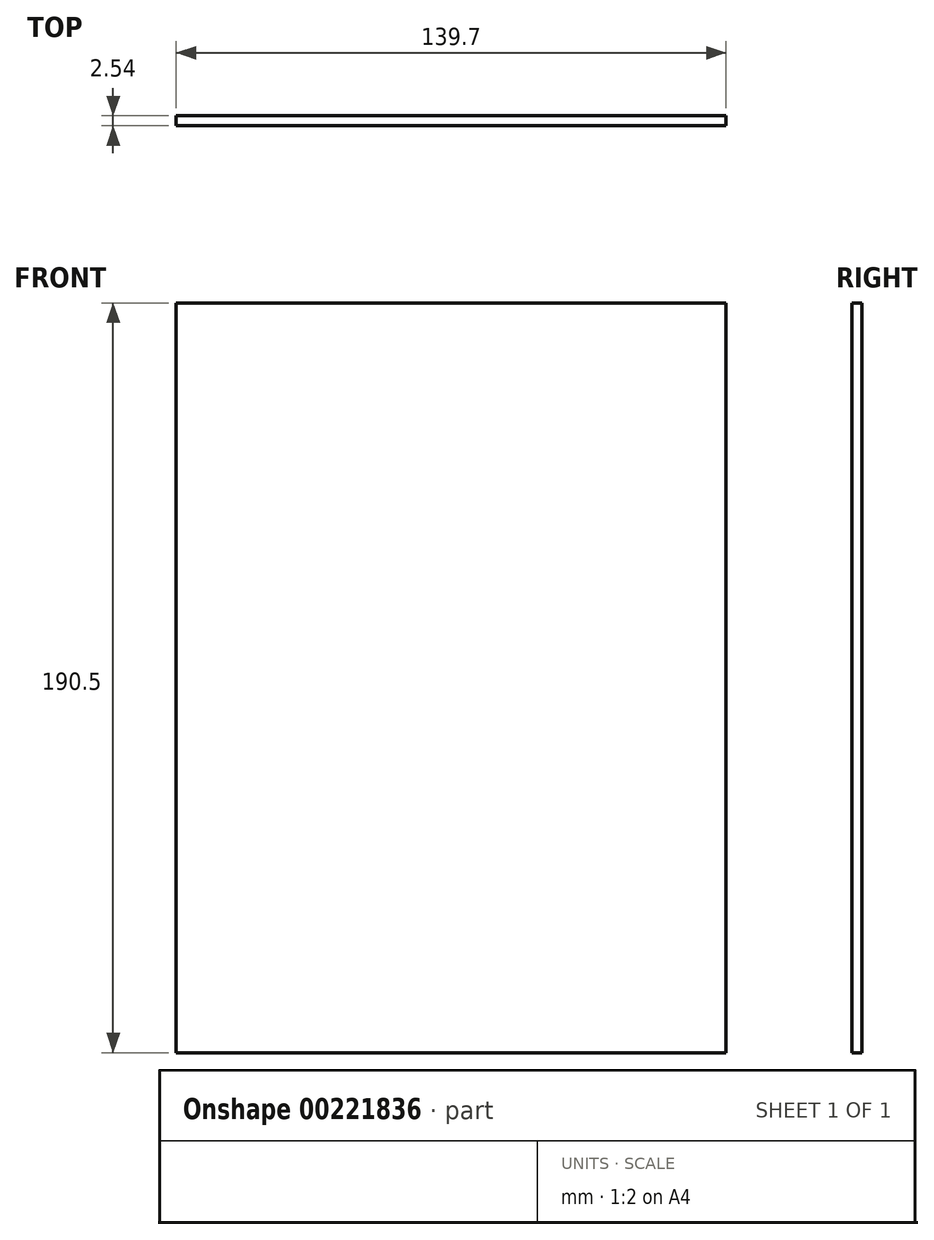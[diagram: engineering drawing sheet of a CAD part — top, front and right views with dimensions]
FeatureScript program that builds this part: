
annotation { "Feature Type Name" : "Feature", "Feature Type Description" : "" }
export const myFeature = defineFeature(function(context is Context, id is Id, definition is map)
    precondition{}
    {
        {
            var Q0;
            Q0=qCreatedBy(makeId("Front.planeOp"),FACE);
            var sketch = newSketch(context, id + "F0", { "sketchPlane" : qUnion([Q0])});
            skLineSegment(sketch, "E0.bottom", {"start": v(69.85, 95.25) * mm, "end": v(-69.85, 95.25) * mm});
            skLineSegment(sketch, "E0.top", {"start": v(69.85, -95.25) * mm, "end": v(-69.85, -95.25) * mm});
            skLineSegment(sketch, "E0.left", {"start": v(69.85, 95.25) * mm, "end": v(69.85, -95.25) * mm});
            skLineSegment(sketch, "E0.right", {"start": v(-69.85, 95.25) * mm, "end": v(-69.85, -95.25) * mm});
            skPoint(sketch, "E0.middle", {"position": v(0, 0) * mm});
            skSolve(sketch);
        }
        {
            var Q0;
            Q0 = qSketchRegion(id + "F0", true);
            extrude(context, id + "F1", {"entities" : qUnion([Q0]), "depth" : 2.54 * mm});
        }
    });
